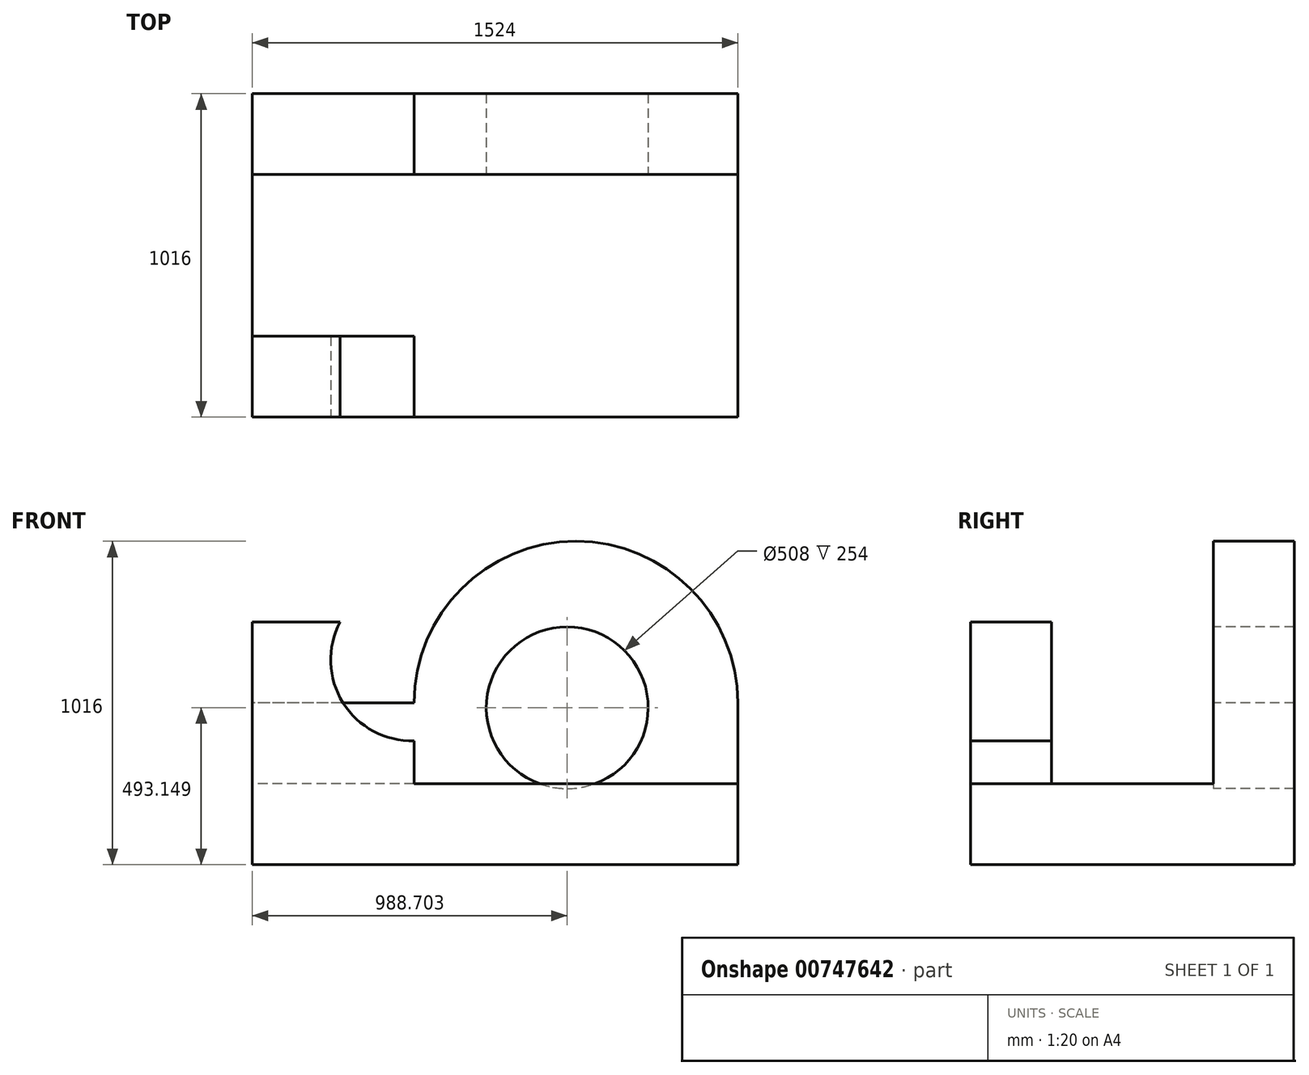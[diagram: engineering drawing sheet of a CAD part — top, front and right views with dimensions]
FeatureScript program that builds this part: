
annotation { "Feature Type Name" : "Feature", "Feature Type Description" : "" }
export const myFeature = defineFeature(function(context is Context, id is Id, definition is map)
    precondition{}
    {
        {
            var Q0;
            Q0=qCreatedBy(makeId("Front.planeOp"),FACE);
            var sketch = newSketch(context, id + "F0", { "sketchPlane" : qUnion([Q0])});
            skLineSegment(sketch, "E0", {"start": v(0, 0) * mm, "end": v(1524, 0) * mm});
            skLineSegment(sketch, "E1", {"start": v(1524, 0) * mm, "end": v(1524, 1016) * mm});
            skLineSegment(sketch, "E2", {"start": v(1524, 1016) * mm, "end": v(0, 1016) * mm});
            skLineSegment(sketch, "E3", {"start": v(0, 1016) * mm, "end": v(0, 0) * mm});
            skSolve(sketch);
        }
        {
            var Q0;
            Q0 = qSketchRegion(id + "F0", true);
            extrude(context, id + "F1", {"entities" : qUnion([Q0]), "depth" : 1016 * mm, "offsetDistance" : 25.4 * mm});
        }
        {
            var Q0;
            Q0=makeQuery(id+"F1.opExtrude","CAP_FACE",FACE,{"disambiguationData":[OSD([sQuery(id+"F0.wireOp",EDGE,"E0"),sQuery(id+"F0.wireOp",EDGE,"E1"),sQuery(id+"F0.wireOp",EDGE,"E2"),sQuery(id+"F0.wireOp",EDGE,"E3")])],"isStart":false});
            var sketch = newSketch(context, id + "F2", { "sketchPlane" : qUnion([Q0])});
            skLineSegment(sketch, "E4", {"start": v(508, 1016) * mm, "end": v(508, 254) * mm});
            skLineSegment(sketch, "E5", {"start": v(508, 254) * mm, "end": v(1524, 254) * mm});
            skLineSegment(sketch, "E6", {"start": v(1524, 254) * mm, "end": v(1524, 1016) * mm});
            skLineSegment(sketch, "E7", {"start": v(1524, 1016) * mm, "end": v(508, 1016) * mm});
            skSolve(sketch);
        }
        {
            var Q0;
            Q0 = qSketchRegion(id + "F2", true);
            extrude(context, id + "F3", {"entities" : qUnion([Q0]), "operationType" : NewBodyOperationType.REMOVE, "oppositeDirection" : true, "depth" : 254 * mm, "offsetDistance" : 25.4 * mm});
        }
        {
            var Q0;
            Q0=makeQuery(id+"F1.opExtrude","SWEPT_FACE",FACE,{"disambiguationData":[OSD([sQuery(id+"F0.wireOp",EDGE,"E2")])]});
            var sketch = newSketch(context, id + "F4", { "sketchPlane" : qUnion([Q0])});
            skLineSegment(sketch, "E8", {"start": v(508, -762) * mm, "end": v(0, -762) * mm});
            skLineSegment(sketch, "E9", {"start": v(0, -762) * mm, "end": v(0, -254) * mm});
            skLineSegment(sketch, "E10", {"start": v(0, -254) * mm, "end": v(1524, -254) * mm});
            skLineSegment(sketch, "E11", {"start": v(1524, -254) * mm, "end": v(1524, -762) * mm});
            skLineSegment(sketch, "E12", {"start": v(1524, -762) * mm, "end": v(0, -762) * mm});
            skSolve(sketch);
        }
        {
            var Q0;
            Q0 = qSketchRegion(id + "F4", true);
            extrude(context, id + "F5", {"entities" : qUnion([Q0]), "operationType" : NewBodyOperationType.REMOVE, "oppositeDirection" : true, "depth" : 762 * mm, "offsetDistance" : 25.4 * mm});
        }
        {
            var Q0;
            Q0=makeQuery(id+"F1.opExtrude","CAP_FACE",FACE,{"disambiguationData":[OSD([sQuery(id+"F0.wireOp",EDGE,"E0"),sQuery(id+"F0.wireOp",EDGE,"E1"),sQuery(id+"F0.wireOp",EDGE,"E2"),sQuery(id+"F0.wireOp",EDGE,"E3")])],"isStart":false});
            var sketch = newSketch(context, id + "F6", { "sketchPlane" : qUnion([Q0])});
            skLineSegment(sketch, "E13", {"start": v(0, 1016) * mm, "end": v(508, 1016) * mm});
            skLineSegment(sketch, "E14", {"start": v(508, 1016) * mm, "end": v(508, 762) * mm});
            skLineSegment(sketch, "E15", {"start": v(508, 762) * mm, "end": v(0, 762) * mm});
            skLineSegment(sketch, "E16", {"start": v(0, 762) * mm, "end": v(0, 1016) * mm});
            skSolve(sketch);
        }
        {
            var Q0;
            Q0 = qSketchRegion(id + "F6", true);
            extrude(context, id + "F7", {"entities" : qUnion([Q0]), "operationType" : NewBodyOperationType.REMOVE, "oppositeDirection" : true, "depth" : 254 * mm, "offsetDistance" : 25.4 * mm});
        }
        {
            var Q0;
            Q0=makeQuery(id+"F5.boolean.opBoolean","COPY",FACE,{"derivedFrom":makeQuery(id+"F5.opExtrude","SWEPT_FACE",FACE,{"disambiguationData":[OSD([sQuery(id+"F4.wireOp",EDGE,"E10")])]})});
            var sketch = newSketch(context, id + "F8", { "sketchPlane" : qUnion([Q0])});
            skLineSegment(sketch, "E17", {"start": v(0, 1016) * mm, "end": v(508, 1016) * mm});
            skLineSegment(sketch, "E18", {"start": v(508, 1016) * mm, "end": v(508, 508) * mm});
            skLineSegment(sketch, "E19", {"start": v(508, 508) * mm, "end": v(0, 508) * mm});
            skLineSegment(sketch, "E20", {"start": v(0, 508) * mm, "end": v(0, 1016) * mm});
            skSolve(sketch);
        }
        {
            var Q0;
            Q0 = qSketchRegion(id + "F8", true);
            extrude(context, id + "F9", {"entities" : qUnion([Q0]), "operationType" : NewBodyOperationType.REMOVE, "oppositeDirection" : true, "depth" : 254 * mm, "offsetDistance" : 25.4 * mm});
        }
        {
            var Q0;
            Q0=makeQuery(id+"F5.boolean.opBoolean","COPY",FACE,{"derivedFrom":makeQuery(id+"F5.opExtrude","SWEPT_FACE",FACE,{"disambiguationData":[OSD([sQuery(id+"F4.wireOp",EDGE,"E10")])]})});
            var sketch = newSketch(context, id + "F10", { "sketchPlane" : qUnion([Q0])});
            skLineSegment(sketch, "E21", {"start": v(508, 508) * mm, "end": v(508, 1016) * mm});
            skLineSegment(sketch, "E22", {"start": v(508, 1016) * mm, "end": v(1524, 1016) * mm});
            skLineSegment(sketch, "E23", {"start": v(1524, 1016) * mm, "end": v(1524, 508) * mm});
            skArc(sketch, "E24", {"start": v(1524, 508) * mm, "mid": v(1016, 1016) * mm, "end": v(508, 508) * mm});
            skSolve(sketch);
        }
        {
            var Q0;
            Q0 = qSketchRegion(id + "F10", true);
            extrude(context, id + "F11", {"entities" : qUnion([Q0]), "operationType" : NewBodyOperationType.REMOVE, "oppositeDirection" : true, "depth" : 254 * mm, "offsetDistance" : 25.4 * mm});
        }
        {
            var Q0;
            Q0=makeQuery(id+"F5.boolean.opBoolean","COPY",FACE,{"derivedFrom":makeQuery(id+"F5.opExtrude","SWEPT_FACE",FACE,{"disambiguationData":[OSD([sQuery(id+"F4.wireOp",EDGE,"E10")])]})});
            var sketch = newSketch(context, id + "F12", { "sketchPlane" : qUnion([Q0])});
            skCircle(sketch, "E25", {"center": v(988.7, 493.15) * mm, "radius": 254 * mm});
            skSolve(sketch);
        }
        {
            var Q0;
            Q0 = qSketchRegion(id + "F12", true);
            extrude(context, id + "F13", {"entities" : qUnion([Q0]), "operationType" : NewBodyOperationType.REMOVE, "oppositeDirection" : true, "depth" : 254 * mm, "offsetDistance" : 25.4 * mm});
        }
        {
            var Q0;
            Q0=makeQuery(id+"F1.opExtrude","CAP_FACE",FACE,{"disambiguationData":[OSD([sQuery(id+"F0.wireOp",EDGE,"E0"),sQuery(id+"F0.wireOp",EDGE,"E1"),sQuery(id+"F0.wireOp",EDGE,"E2"),sQuery(id+"F0.wireOp",EDGE,"E3")])],"isStart":false});
            var sketch = newSketch(context, id + "F14", { "sketchPlane" : qUnion([Q0])});
            skLineSegment(sketch, "E26", {"start": v(275.64, 762) * mm, "end": v(508, 762) * mm});
            skLineSegment(sketch, "E27", {"start": v(508, 762) * mm, "end": v(508, 389.6) * mm});
            skArc(sketch, "E28", {"start": v(275.64, 762) * mm, "mid": v(284.8, 509.02) * mm, "end": v(508, 389.6) * mm});
            skSolve(sketch);
        }
        {
            var Q0;
            Q0 = qSketchRegion(id + "F14", true);
            extrude(context, id + "F15", {"entities" : qUnion([Q0]), "operationType" : NewBodyOperationType.REMOVE, "oppositeDirection" : true, "depth" : 254 * mm, "offsetDistance" : 25.4 * mm});
        }
    });
